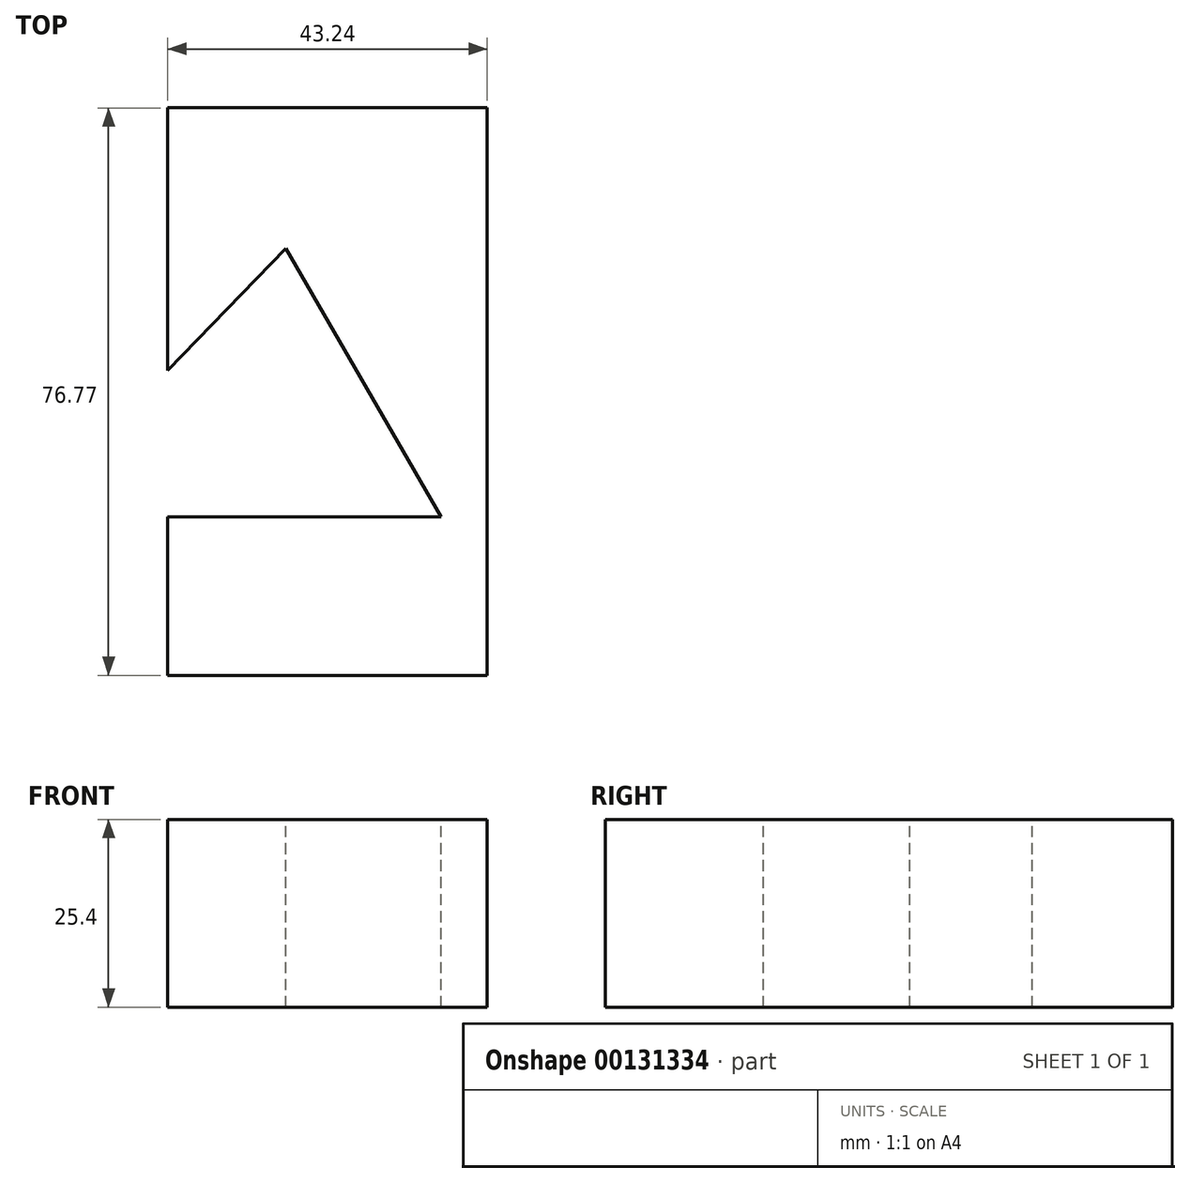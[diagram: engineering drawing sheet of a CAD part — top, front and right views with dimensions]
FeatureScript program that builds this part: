
annotation { "Feature Type Name" : "Feature", "Feature Type Description" : "" }
export const myFeature = defineFeature(function(context is Context, id is Id, definition is map)
    precondition{}
    {
        {
            var Q0;
            Q0=qCreatedBy(makeId("Top.planeOp"),FACE);
            var sketch = newSketch(context, id + "F0", { "sketchPlane" : qUnion([Q0])});
            skLineSegment(sketch, "E0", {"start": v(-17.43, 39.85) * mm, "end": v(-17.43, 4.3) * mm});
            skLineSegment(sketch, "E1", {"start": v(-17.43, -15.5) * mm, "end": v(-17.43, -36.92) * mm});
            skLineSegment(sketch, "E2", {"start": v(-17.43, 4.3) * mm, "end": v(-1.46, 20.86) * mm});
            skLineSegment(sketch, "E3", {"start": v(-1.46, 20.86) * mm, "end": v(19.55, -15.5) * mm});
            skLineSegment(sketch, "E4", {"start": v(19.55, -15.5) * mm, "end": v(-17.43, -15.5) * mm});
            skLineSegment(sketch, "E5", {"start": v(-17.43, -36.92) * mm, "end": v(25.81, -36.92) * mm});
            skLineSegment(sketch, "E6", {"start": v(25.81, -36.92) * mm, "end": v(25.81, 39.85) * mm});
            skLineSegment(sketch, "E7", {"start": v(25.81, 39.85) * mm, "end": v(-17.43, 39.85) * mm});
            skSolve(sketch);
        }
        {
            var Q0;
            Q0=sQuery(id+"F0.wireOp",EDGE,"E0");
            var Q1;
            Q1=sQuery(id+"F0.wireOp",EDGE,"E1");
            var Q2;
            Q2=sQuery(id+"F0.wireOp",EDGE,"E2");
            var Q3;
            Q3=sQuery(id+"F0.wireOp",EDGE,"E3");
            var Q4;
            Q4=sQuery(id+"F0.wireOp",EDGE,"E4");
            var Q5;
            Q5=sQuery(id+"F0.wireOp",EDGE,"E5");
            var Q6;
            Q6=sQuery(id+"F0.wireOp",EDGE,"E6");
            var Q7;
            Q7=sQuery(id+"F0.wireOp",EDGE,"E7");
            extrude(context, id + "F1", {"bodyType" : ToolBodyType.SURFACE, "surfaceEntities" : qUnion([Q0, Q1, Q2, Q3, Q4, Q5, Q6, Q7]), "depth" : 25.4 * mm});
        }
    });
